# Revit family: GR_Щелевой диффузор линейный_TLL_Приток_R21
name_source: partatom
category: Воздухораспределители
units: mm (PartAtom-declared; Revit-internal decimal feet)

## family parameters
Всегда вертикально = Да
Заголовок OmniClass = Diffusers, Registers, and Grilles
На основе рабочей плоскости = Нет
Номер OmniClass = 23.75.70.21.27.11
Общий = Нет
При загрузке вырезать с полостями = Да
Размер круглого соединителя = Использовать диаметр
Тип детали = Нормальный
Точка принадлежности помещению = Да

## types (2) — shared parameters
ADSK_URL страницы изделия = https://grilles.ru
ADSK_Автор = THE GRILLES
ADSK_Версия Revit = 2021
ADSK_Группирование = TL
ADSK_Единица измерения = шт.
ADSK_Завод-изготовитель = ООО "ВЕНТРЕШЕТКИКОМ"
ADSK_Код изделия = 000202
ADSK_Количество = 1
GR_Внутреннее исполнение = Алюминий, RAL 9005M, черный
GR_Материал корпуса = Алюминий, RAL 9016M, белый
URL = https://grilles.ru
Заглушка_Толщина = 1 мм
Изготовитель = ООО "ВЕНТРЕШЕТКИКОМ"
Макс.Длина = 2900 мм
Мин.Длина = 200 мм
Описание = Линейный щелевой диффузор TL предназначен для скрытой установки в систему вентиляции и кондиционирования в качестве конечного декоративного элемента инженерной системы в жилых, торговых, и офисных помещениях. Диффузоры встраиваются в стены или потолок, изготавливаемые из гипсокартона и металлического каркаса.
Отступ_Несущей_Рамы = 50 мм
zero-valued in all types: Отметка по умолчанию

## per-type parameters (varying)
| type | ADSK_Размер_Ширина | Расстояние между ламелями(КРВ,ВПВ) | Расстояние между ламелями(Кронштейн) | Щель_Ширина(По каталогу) |
| TLL 60 | 196 мм | 196 мм | 170 мм | 60 мм |
| TLL 70 | 206 мм | 206 мм | 180 мм | 70 мм |

note: column(s) folded — value = type name in every type: ADSK_Марка
